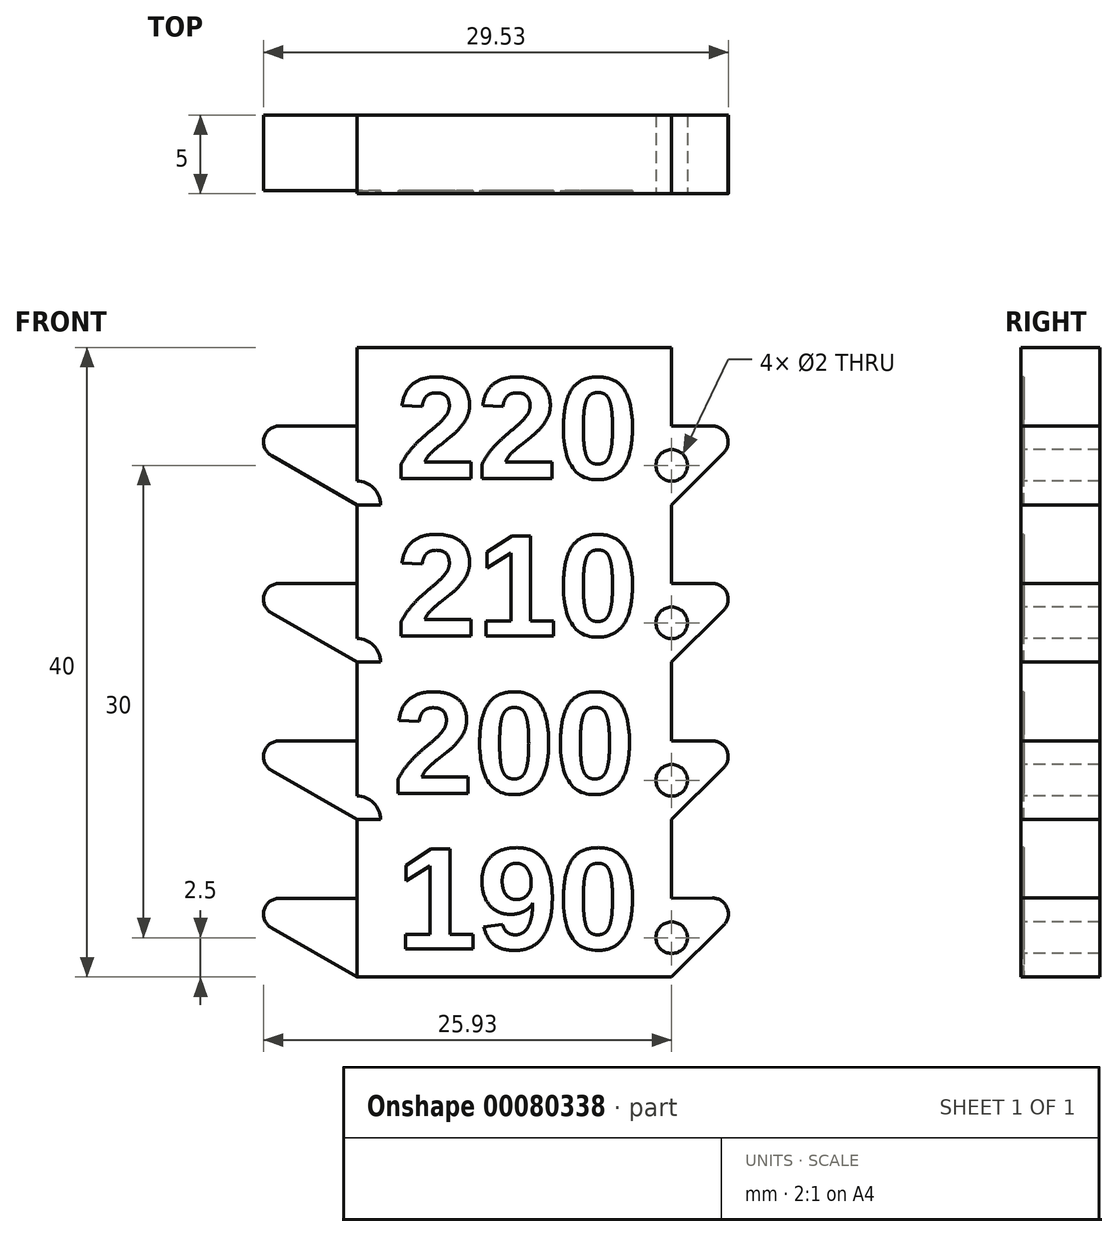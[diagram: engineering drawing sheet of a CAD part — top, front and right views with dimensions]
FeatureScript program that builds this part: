
annotation { "Feature Type Name" : "Feature", "Feature Type Description" : "" }
export const myFeature = defineFeature(function(context is Context, id is Id, definition is map)
    precondition{}
    {
        {
            var Q0;
            Q0=qCreatedBy(makeId("Top.planeOp"),FACE);
            var sketch = newSketch(context, id + "F0", { "sketchPlane" : qUnion([Q0])});
            skLineSegment(sketch, "E0.bottom", {"start": v(-10, 2.5) * mm, "end": v(-7, 2.5) * mm});
            skLineSegment(sketch, "E0.top", {"start": v(-10, -2.5) * mm, "end": v(10, -2.5) * mm});
            skLineSegment(sketch, "E0.left", {"start": v(-10, 2.5) * mm, "end": v(-10, -2.5) * mm});
            skLineSegment(sketch, "E0.right", {"start": v(10, 2.5) * mm, "end": v(10, -2.5) * mm});
            skPoint(sketch, "E0.middle", {"position": v(0, 0) * mm});
            skLineSegment(sketch, "E1.trimOffspring", {"start": v(7, 2.5) * mm, "end": v(10, 2.5) * mm});
            skLineSegment(sketch, "E2", {"start": v(-7, 2.5) * mm, "end": v(7, 2.5) * mm});
            skPoint(sketch, "E3.left.end.orphan", {"position": v(-7, 0.5) * mm});
            skPoint(sketch, "E3.left.start.orphan", {"position": v(-7, -0.5) * mm});
            skPoint(sketch, "E3.right.end.orphan", {"position": v(7, 0.5) * mm});
            skPoint(sketch, "E3.right.start.orphan", {"position": v(7, -0.5) * mm});
            skSolve(sketch);
        }
        {
            var Q0;
            Q0 = qSketchRegion(id + "F0", true);
            extrude(context, id + "F1", {"entities" : qUnion([Q0]), "depth" : 40 * mm});
        }
        {
            var Q0;
            Q0=makeQuery(id+"F1.opExtrude","SWEPT_FACE",FACE,{"disambiguationData":[OSD([sQuery(id+"F0.wireOp",EDGE,"E0.top")])]});
            var sketch = newSketch(context, id + "F2", { "sketchPlane" : qUnion([Q0])});
            skLineSegment(sketch, "E4", {"start": v(-10, 10) * mm, "end": v(10, 10) * mm});
            skLineSegment(sketch, "E5", {"start": v(-10, 20) * mm, "end": v(10, 20) * mm});
            skLineSegment(sketch, "E6", {"start": v(-10, 30) * mm, "end": v(10, 30) * mm});
            skArc(sketch, "E7", {"start": v(-8.5, 10) * mm, "mid": v(-8.94, 11.06) * mm, "end": v(-10, 11.5) * mm});
            skArc(sketch, "E8", {"start": v(-8.5, 20) * mm, "mid": v(-8.94, 21.06) * mm, "end": v(-10, 21.5) * mm});
            skArc(sketch, "E9", {"start": v(-8.5, 30) * mm, "mid": v(-8.94, 31.06) * mm, "end": v(-10, 31.5) * mm});
            skText(sketch, "E10", { "text": "190\n", "fontName": "Arimo-Bold.ttf"});
            skPoint(sketch, "E11", {"position": v(-7.5, 5.1) * mm});
            skLineSegment(sketch, "E12.0", {"start": v(-10, 40) * mm, "end": v(-10, 0) * mm});
            skLineSegment(sketch, "E13", {"start": v(-10, 0) * mm, "end": v(-10, 10) * mm});
            skLineSegment(sketch, "E14", {"start": v(-10, 10) * mm, "end": v(-10, 20) * mm});
            skLineSegment(sketch, "E15", {"start": v(-10, 20) * mm, "end": v(-10, 30) * mm});
            skLineSegment(sketch, "E16", {"start": v(-10, 30) * mm, "end": v(-10, 40) * mm});
            skPoint(sketch, "E17", {"position": v(-10, 35) * mm});
            skPoint(sketch, "E18", {"position": v(-10, 25) * mm});
            skPoint(sketch, "E19", {"position": v(-10, 15) * mm});
            skPoint(sketch, "E20", {"position": v(-10, 5) * mm});
            skText(sketch, "E21", { "text": "200", "fontName": "Arimo-Bold.ttf"});
            skPoint(sketch, "E22", {"position": v(-7.69, 15) * mm});
            skText(sketch, "E23", { "text": "210", "fontName": "Arimo-Bold.ttf"});
            skPoint(sketch, "E24", {"position": v(-7.5, 25) * mm});
            skText(sketch, "E25", { "text": "220\n", "fontName": "Arimo-Bold.ttf"});
            skPoint(sketch, "E26", {"position": v(-7.5, 35) * mm});
            skLineSegment(sketch, "E27", {"start": v(-10, 0) * mm, "end": v(-18.66, 5) * mm});
            skLineSegment(sketch, "E28", {"start": v(-10, 10) * mm, "end": v(-18.66, 15) * mm});
            skLineSegment(sketch, "E29", {"start": v(-10, 20) * mm, "end": v(-18.66, 25) * mm});
            skLineSegment(sketch, "E30", {"start": v(-10, 30) * mm, "end": v(-18.66, 35) * mm});
            skLineSegment(sketch, "E31", {"start": v(-10, 35) * mm, "end": v(-18.66, 35) * mm});
            skLineSegment(sketch, "E32", {"start": v(-10, 25) * mm, "end": v(-18.66, 25) * mm});
            skLineSegment(sketch, "E33", {"start": v(-10, 15) * mm, "end": v(-18.66, 15) * mm});
            skLineSegment(sketch, "E34", {"start": v(-10, 5) * mm, "end": v(-18.66, 5) * mm});
            skLineSegment(sketch, "E35", {"start": v(10, 0) * mm, "end": v(15.03, 5.03) * mm});
            skLineSegment(sketch, "E36", {"start": v(10, 10) * mm, "end": v(15, 15) * mm});
            skLineSegment(sketch, "E37", {"start": v(10, 20) * mm, "end": v(15, 25) * mm});
            skLineSegment(sketch, "E38", {"start": v(10, 30) * mm, "end": v(15, 35) * mm});
            skLineSegment(sketch, "E39", {"start": v(10, 25) * mm, "end": v(15, 25) * mm});
            skPoint(sketch, "E39.startSnap0", {"position": v(7.5, 25) * mm});
            skLineSegment(sketch, "E40", {"start": v(10, 35) * mm, "end": v(15, 35) * mm});
            skPoint(sketch, "E40.startSnap0", {"position": v(7.5, 35) * mm});
            skLineSegment(sketch, "E41", {"start": v(10, 15) * mm, "end": v(15, 15) * mm});
            skLineSegment(sketch, "E42", {"start": v(10, 5) * mm, "end": v(15.03, 5.03) * mm});
            skPoint(sketch, "E43.orphan", {"position": v(25.52, 5.1) * mm});
            skCircle(sketch, "E44", {"center": v(10, 2.5) * mm, "radius": 1 * mm});
            skCircle(sketch, "E45", {"center": v(10, 12.5) * mm, "radius": 1 * mm});
            skCircle(sketch, "E46", {"center": v(10, 22.5) * mm, "radius": 1 * mm});
            skCircle(sketch, "E47", {"center": v(10, 32.5) * mm, "radius": 1 * mm});
            skLineSegment(sketch, "E48.trimOffspring", {"start": v(10, 31.5) * mm, "end": v(10, 30) * mm});
            skLineSegment(sketch, "E49.trimOffspring", {"start": v(10, 21.5) * mm, "end": v(10, 20) * mm});
            skLineSegment(sketch, "E50.trimOffspring", {"start": v(10, 11.5) * mm, "end": v(10, 10) * mm});
            skLineSegment(sketch, "E51.trimOffspring", {"start": v(10, 1.5) * mm, "end": v(10, 0) * mm});
            const initialGuessF2  = {"E10": [-0.0075, 0.00178, 1, 0, 0.00664], "E21": [-0.00769, 0.01168, 1, 0, 0.00664], "E23": [-0.0075, 0.02168, 1, 0, 0.00664], "E25": [-0.0075, 0.03168, 1, 0, 0.00664]};
            skSetInitialGuess(sketch, initialGuessF2);
            skSolve(sketch);
        }
        {
            var Q0;
            {var subQ3=sQuery(id+"F2.wireOp",EDGE,"E30");Q0=makeQuery(id+"F2.imprint","IMPRINT",FACE,{"disambiguationData":[TD([[makeQuery(id+"F2.imprint","IMPRINT",EDGE,{"derivedFrom":subQ3}),-1.0]])]});}
            var Q1;
            {var subQ3=sQuery(id+"F2.wireOp",EDGE,"E29");Q1=makeQuery(id+"F2.imprint","IMPRINT",FACE,{"disambiguationData":[TD([[makeQuery(id+"F2.imprint","IMPRINT",EDGE,{"derivedFrom":subQ3}),-1.0]])]});}
            var Q2;
            {var subQ0=sQuery(id+"F2.wireOp",EDGE,"E37");Q2=makeQuery(id+"F2.imprint","IMPRINT",FACE,{"disambiguationData":[TD([[makeQuery(id+"F2.imprint","IMPRINT",EDGE,{"derivedFrom":subQ0}),1.0]])]});}
            var Q3;
            {var subQ3=sQuery(id+"F2.wireOp",EDGE,"E28");Q3=makeQuery(id+"F2.imprint","IMPRINT",FACE,{"disambiguationData":[TD([[makeQuery(id+"F2.imprint","IMPRINT",EDGE,{"derivedFrom":subQ3}),-1.0]])]});}
            var Q4;
            {var subQ0=sQuery(id+"F2.wireOp",EDGE,"E27");Q4=makeQuery(id+"F2.imprint","IMPRINT",FACE,{"disambiguationData":[TD([[makeQuery(id+"F2.imprint","IMPRINT",EDGE,{"derivedFrom":subQ0}),-1.0]])]});}
            var Q5;
            {var subQ0=sQuery(id+"F2.wireOp",EDGE,"E36");Q5=makeQuery(id+"F2.imprint","IMPRINT",FACE,{"disambiguationData":[TD([[makeQuery(id+"F2.imprint","IMPRINT",EDGE,{"derivedFrom":subQ0}),1.0]])]});}
            var Q6;
            {var subQ0=sQuery(id+"F2.wireOp",EDGE,"E38");Q6=makeQuery(id+"F2.imprint","IMPRINT",FACE,{"disambiguationData":[TD([[makeQuery(id+"F2.imprint","IMPRINT",EDGE,{"derivedFrom":subQ0}),1.0]])]});}
            var Q7;
            {var subQ0=sQuery(id+"F2.wireOp",EDGE,"E35");Q7=makeQuery(id+"F2.imprint","IMPRINT",FACE,{"disambiguationData":[TD([[makeQuery(id+"F2.imprint","IMPRINT",EDGE,{"derivedFrom":subQ0}),1.0]])]});}
            extrude(context, id + "F3", {"entities" : qUnion([Q0, Q1, Q2, Q3, Q4, Q5, Q6, Q7]), "operationType" : NewBodyOperationType.ADD, "oppositeDirection" : true, "depth" : 5 * mm});
        }
        {
            var Q0;
            Q0 = qSketchRegion(id + "F2", true);
            extrude(context, id + "F4", {"entities" : qUnion([Q0]), "operationType" : NewBodyOperationType.REMOVE, "oppositeDirection" : true, "depth" : 0.2 * mm});
        }
        {
            var Q0;
            Q0=makeQuery(id+"F3.opExtrude","SWEPT_EDGE",EDGE,{"disambiguationData":[OSD([sQuery(id+"F2.wireOp",EDGE,"E38"),sQuery(id+"F2.wireOp",EDGE,"E40")])]});
            var Q1;
            Q1=makeQuery(id+"F3.opExtrude","SWEPT_EDGE",EDGE,{"disambiguationData":[OSD([sQuery(id+"F2.wireOp",EDGE,"E37"),sQuery(id+"F2.wireOp",EDGE,"E39")])]});
            var Q2;
            Q2=makeQuery(id+"F3.opExtrude","SWEPT_EDGE",EDGE,{"disambiguationData":[OSD([sQuery(id+"F2.wireOp",EDGE,"E36"),sQuery(id+"F2.wireOp",EDGE,"E41")])]});
            var Q3;
            Q3=makeQuery(id+"F3.opExtrude","SWEPT_EDGE",EDGE,{"disambiguationData":[OSD([sQuery(id+"F2.wireOp",EDGE,"E35"),sQuery(id+"F2.wireOp",EDGE,"E42")])]});
            var Q4;
            Q4=makeQuery(id+"F3.opExtrude","SWEPT_EDGE",EDGE,{"disambiguationData":[OSD([sQuery(id+"F2.wireOp",EDGE,"E27"),sQuery(id+"F2.wireOp",EDGE,"E34")])]});
            var Q5;
            Q5=makeQuery(id+"F3.opExtrude","SWEPT_EDGE",EDGE,{"disambiguationData":[OSD([sQuery(id+"F2.wireOp",EDGE,"E28"),sQuery(id+"F2.wireOp",EDGE,"E33")])]});
            var Q6;
            Q6=makeQuery(id+"F3.opExtrude","SWEPT_EDGE",EDGE,{"disambiguationData":[OSD([sQuery(id+"F2.wireOp",EDGE,"E29"),sQuery(id+"F2.wireOp",EDGE,"E32")])]});
            var Q7;
            Q7=makeQuery(id+"F3.opExtrude","SWEPT_EDGE",EDGE,{"disambiguationData":[OSD([sQuery(id+"F2.wireOp",EDGE,"E30"),sQuery(id+"F2.wireOp",EDGE,"E31")])]});
            fillet(context, id + "F5", {"entities" : qUnion([Q0, Q1, Q2, Q3, Q4, Q5, Q6, Q7]), "radius" : 1 * mm, "allowEdgeOverflow" : false});
        }
        {
            var Q0;
            {var subQ0=sQuery(id+"F2.wireOp",EDGE,"E47");var subQ1=makeQuery(id+"F1.opExtrude","SWEPT_EDGE",EDGE,{"disambiguationData":[OSD([sQuery(id+"F0.wireOp",EDGE,"E0.top"),sQuery(id+"F0.wireOp",EDGE,"E0.right")])]});var subQ3=makeQuery(id+"F2.imprint","INTERSECT",VERTEX,{"derivedFrom":[subQ1,subQ0]});Q0=makeQuery(id+"F2.imprint","IMPRINT",FACE,{"disambiguationData":[TD([[makeQuery(id+"F2.imprint","IMPRINT",EDGE,{"disambiguationData":[TD([[subQ3,-1.0]])],"derivedFrom":subQ0}),1.0]])]});}
            var Q1;
            {var subQ0=sQuery(id+"F2.wireOp",EDGE,"E46");var subQ1=makeQuery(id+"F1.opExtrude","SWEPT_EDGE",EDGE,{"disambiguationData":[OSD([sQuery(id+"F0.wireOp",EDGE,"E0.top"),sQuery(id+"F0.wireOp",EDGE,"E0.right")])]});var subQ3=makeQuery(id+"F2.imprint","INTERSECT",VERTEX,{"derivedFrom":[subQ1,subQ0]});Q1=makeQuery(id+"F2.imprint","IMPRINT",FACE,{"disambiguationData":[TD([[makeQuery(id+"F2.imprint","IMPRINT",EDGE,{"disambiguationData":[TD([[subQ3,-1.0]])],"derivedFrom":subQ0}),1.0]])]});}
            var Q2;
            {var subQ0=sQuery(id+"F2.wireOp",EDGE,"E45");var subQ1=makeQuery(id+"F1.opExtrude","SWEPT_EDGE",EDGE,{"disambiguationData":[OSD([sQuery(id+"F0.wireOp",EDGE,"E0.top"),sQuery(id+"F0.wireOp",EDGE,"E0.right")])]});var subQ3=makeQuery(id+"F2.imprint","INTERSECT",VERTEX,{"derivedFrom":[subQ1,subQ0]});Q2=makeQuery(id+"F2.imprint","IMPRINT",FACE,{"disambiguationData":[TD([[makeQuery(id+"F2.imprint","IMPRINT",EDGE,{"disambiguationData":[TD([[subQ3,-1.0]])],"derivedFrom":subQ0}),1.0]])]});}
            var Q3;
            {var subQ0=sQuery(id+"F2.wireOp",EDGE,"E44");var subQ1=makeQuery(id+"F1.opExtrude","SWEPT_EDGE",EDGE,{"disambiguationData":[OSD([sQuery(id+"F0.wireOp",EDGE,"E0.top"),sQuery(id+"F0.wireOp",EDGE,"E0.right")])]});var subQ3=makeQuery(id+"F2.imprint","INTERSECT",VERTEX,{"derivedFrom":[subQ1,subQ0]});Q3=makeQuery(id+"F2.imprint","IMPRINT",FACE,{"disambiguationData":[TD([[makeQuery(id+"F2.imprint","IMPRINT",EDGE,{"disambiguationData":[TD([[subQ3,-1.0]])],"derivedFrom":subQ0}),1.0]])]});}
            extrude(context, id + "F6", {"entities" : qUnion([Q0, Q1, Q2, Q3]), "operationType" : NewBodyOperationType.REMOVE, "endBound" : BoundingType.THROUGH_ALL, "oppositeDirection" : true, "depth" : 25 * mm});
        }
    });
